# Revit family: L500xH1200_GRYFIT NEO, Multiblade fire damper
name_source: partatom
category: Duct Accessories
units: mm (PartAtom-declared; Revit-internal decimal feet)

## family parameters
Always vertical = Yes
Cut with Voids When Loaded = No
OmniClass Number = 23.75.70.11.14.14
OmniClass Title = Dampers for Air Ductwork
Part Type = Damper
Round Connector Dimension = Use Diameter
Shared = No
Work Plane-Based = No

## types (1)
- GRYFIT NEO, LxH=500x1200,Galvanized steel, KP 20 + WT72C, L=500. H=1200
    95°C = 72°C
    Actuator FDG-8 = No
    Actuator FDG-WT-5 = No
    Actuator FDG-WT-8 = No
    Connector. = Rectangular flange 20 mm
    Damper Length = 150 mm
    Damper Material = <By Category>
    Damper external hight (H1). = 1240
    Damper external width (L1). = 540
    Dimensions as 5 mm in the standard. = No
    Double Beginning and End (2WKKP) = None
    EMS module = No
    Electromagnet = No
    Fire resistance class. = EIS 120
    Gap between grille and damper (G1). = 0
    Geometry = GRYFIT NEO, LxH=500x1200,Galvanized steel, KP 20 + WT72C, L=500. H=1200
    Half Damper Length = 75 mm
    Height (H). = 1200
    Height of mount. hole (Hr). = 1300
    Length (P). = 120
    Material of damper. = Galvanized steel
    Protection grille (TRA) = No
    Type. = GRYFIT NEO
    Width (L). = 500
    Width as 5mm (L 5mm). = 100
    Width of mount. hole (Lr). = 600
    anglXY1 = 180.00°
    anglXY2 = 0.00°
    anglZ1 = 0.00°
    anglZ2 = 0.00°
    heightcon1 = 1200 mm
    heightcon2 = 1200 mm
    lengX1 = 0 mm  [stored 0 ft]
    lengX2 = 60 mm  [stored 0.19685 ft]
    lengXY1 = 600 mm
    lengXY2 = 600 mm
    lengXYZ1 = 500 mm  [stored 1.64042 ft]
    lengXYZ2 = 500 mm  [stored 1.64042 ft]
    lengY1 = 0 mm  [stored 0 ft]
    lengY2 = 0 mm  [stored 0 ft]
    lengZ1 = 0 mm  [stored 0 ft]
    lengZ2 = 0 mm  [stored 0 ft]
    rotcon1 = 0 mm
    rotcon2 = 0 mm
    widthcon1 = 500 mm
    widthcon2 = 500 mm

note: [stored X ft] marks values corroborated as IEEE doubles in the binary element streams (Revit-internal decimal feet)

## geometry (parser evidence)
native form markers: Sweep x4
no freeform markers — native parametric forms only
